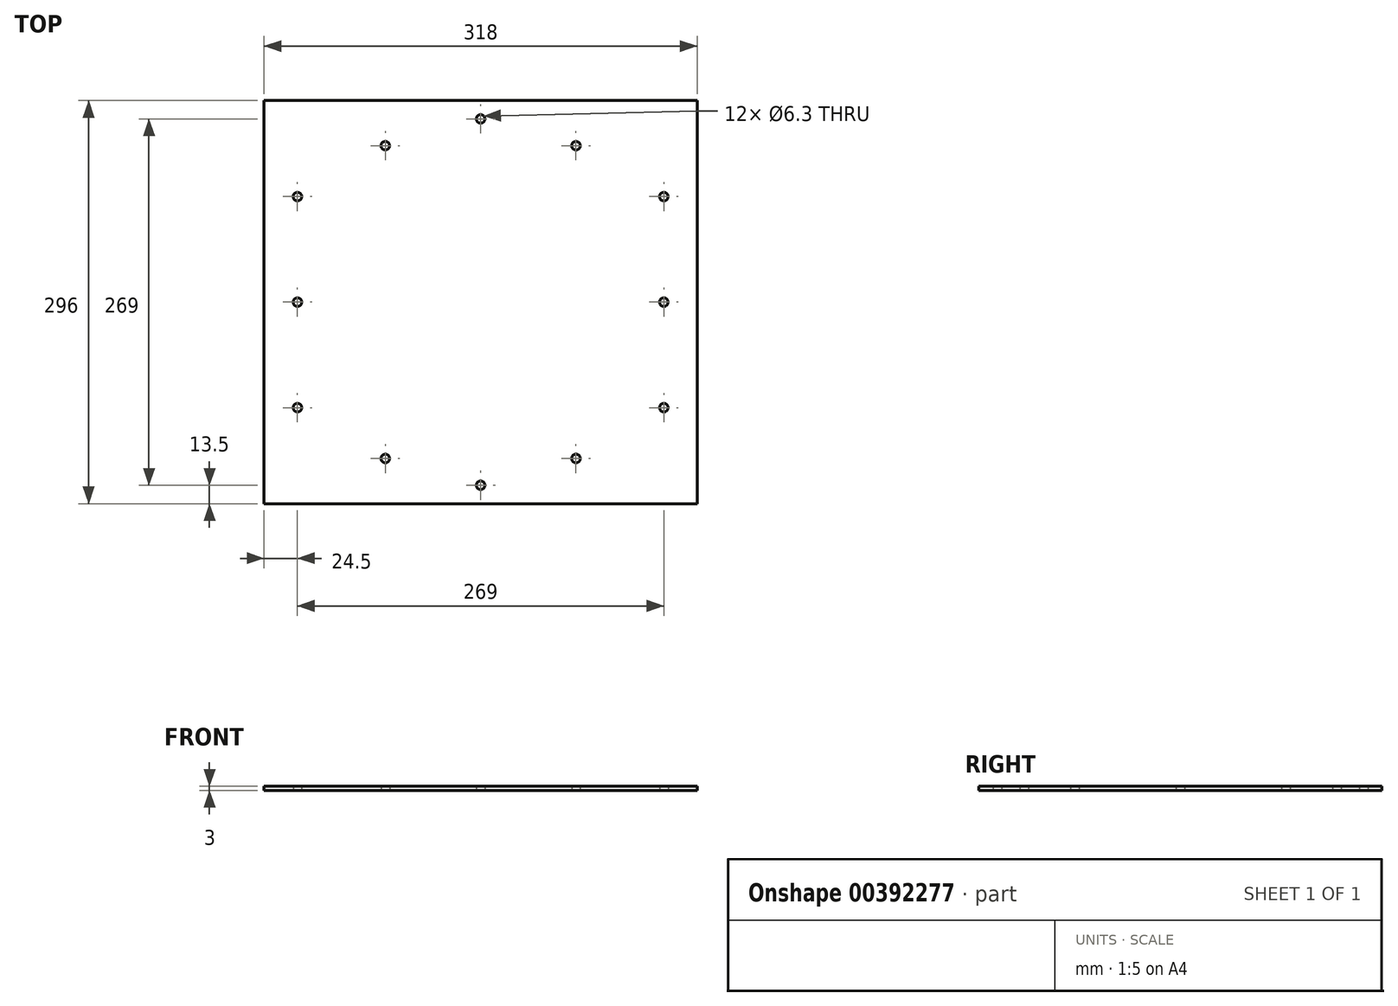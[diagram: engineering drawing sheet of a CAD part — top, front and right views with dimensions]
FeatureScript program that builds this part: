
annotation { "Feature Type Name" : "Feature", "Feature Type Description" : "" }
export const myFeature = defineFeature(function(context is Context, id is Id, definition is map)
    precondition{}
    {
        {
            var Q0;
            Q0=qCreatedBy(makeId("Top.planeOp"),FACE);
            var sketch = newSketch(context, id + "F0", { "sketchPlane" : qUnion([Q0])});
            skLineSegment(sketch, "E0.bottom", {"start": v(159, 148) * mm, "end": v(-159, 148) * mm});
            skLineSegment(sketch, "E0.top", {"start": v(159, -148) * mm, "end": v(-159, -148) * mm});
            skLineSegment(sketch, "E0.left", {"start": v(159, 148) * mm, "end": v(159, -148) * mm});
            skLineSegment(sketch, "E0.right", {"start": v(-159, 148) * mm, "end": v(-159, -148) * mm});
            skPoint(sketch, "E0.middle", {"position": v(0, 0) * mm});
            skLineSegment(sketch, "E1.bottom", {"start": v(-134.5, 77.5) * mm, "end": v(134.5, 77.5) * mm, "construction": true});
            skLineSegment(sketch, "E1.top", {"start": v(-134.5, -77.5) * mm, "end": v(134.5, -77.5) * mm, "construction": true});
            skLineSegment(sketch, "E1.left", {"start": v(-134.5, 77.5) * mm, "end": v(-134.5, -77.5) * mm, "construction": true});
            skLineSegment(sketch, "E1.right", {"start": v(134.5, 77.5) * mm, "end": v(134.5, -77.5) * mm, "construction": true});
            skCircle(sketch, "E2", {"center": v(-134.5, 77.5) * mm, "radius": 3.15 * mm});
            skCircle(sketch, "E3", {"center": v(134.5, 77.5) * mm, "radius": 3.15 * mm});
            skCircle(sketch, "E4", {"center": v(-134.5, -77.5) * mm, "radius": 3.15 * mm});
            skCircle(sketch, "E5", {"center": v(134.5, -77.5) * mm, "radius": 3.15 * mm});
            skPoint(sketch, "E6.startSnap0", {"position": v(0, -148) * mm});
            skPoint(sketch, "E6.endSnap0", {"position": v(0, 77.5) * mm});
            skCircle(sketch, "E7", {"center": v(0, 0) * mm, "radius": 140 * mm, "construction": true});
            skLineSegment(sketch, "E8", {"start": v(0, -148) * mm, "end": v(0, 148) * mm, "construction": true});
            skCircle(sketch, "E9", {"center": v(0, 134.5) * mm, "radius": 3.15 * mm});
            skCircle(sketch, "E10", {"center": v(0, -134.5) * mm, "radius": 3.15 * mm});
            skLineSegment(sketch, "E11", {"start": v(-159, 0) * mm, "end": v(159, 0) * mm, "construction": true});
            skCircle(sketch, "E12", {"center": v(-134.5, 0) * mm, "radius": 3.15 * mm});
            skCircle(sketch, "E13", {"center": v(134.5, 0) * mm, "radius": 3.15 * mm});
            skCircle(sketch, "E14", {"center": v(0, 0) * mm, "radius": 134.5 * mm, "construction": true});
            skCircle(sketch, "E15", {"center": v(-70, 114.85) * mm, "radius": 3.15 * mm});
            skCircle(sketch, "E16", {"center": v(70, 114.85) * mm, "radius": 3.15 * mm});
            skCircle(sketch, "E17", {"center": v(-70, -114.85) * mm, "radius": 3.15 * mm});
            skCircle(sketch, "E18", {"center": v(70, -114.85) * mm, "radius": 3.15 * mm});
            skSolve(sketch);
        }
        {
            var Q0;
            Q0=qSketchRegion(id+"F0",true);
            extrude(context, id + "F1", {"entities" : qUnion([Q0]), "depth" : 3 * mm});
        }
    });
